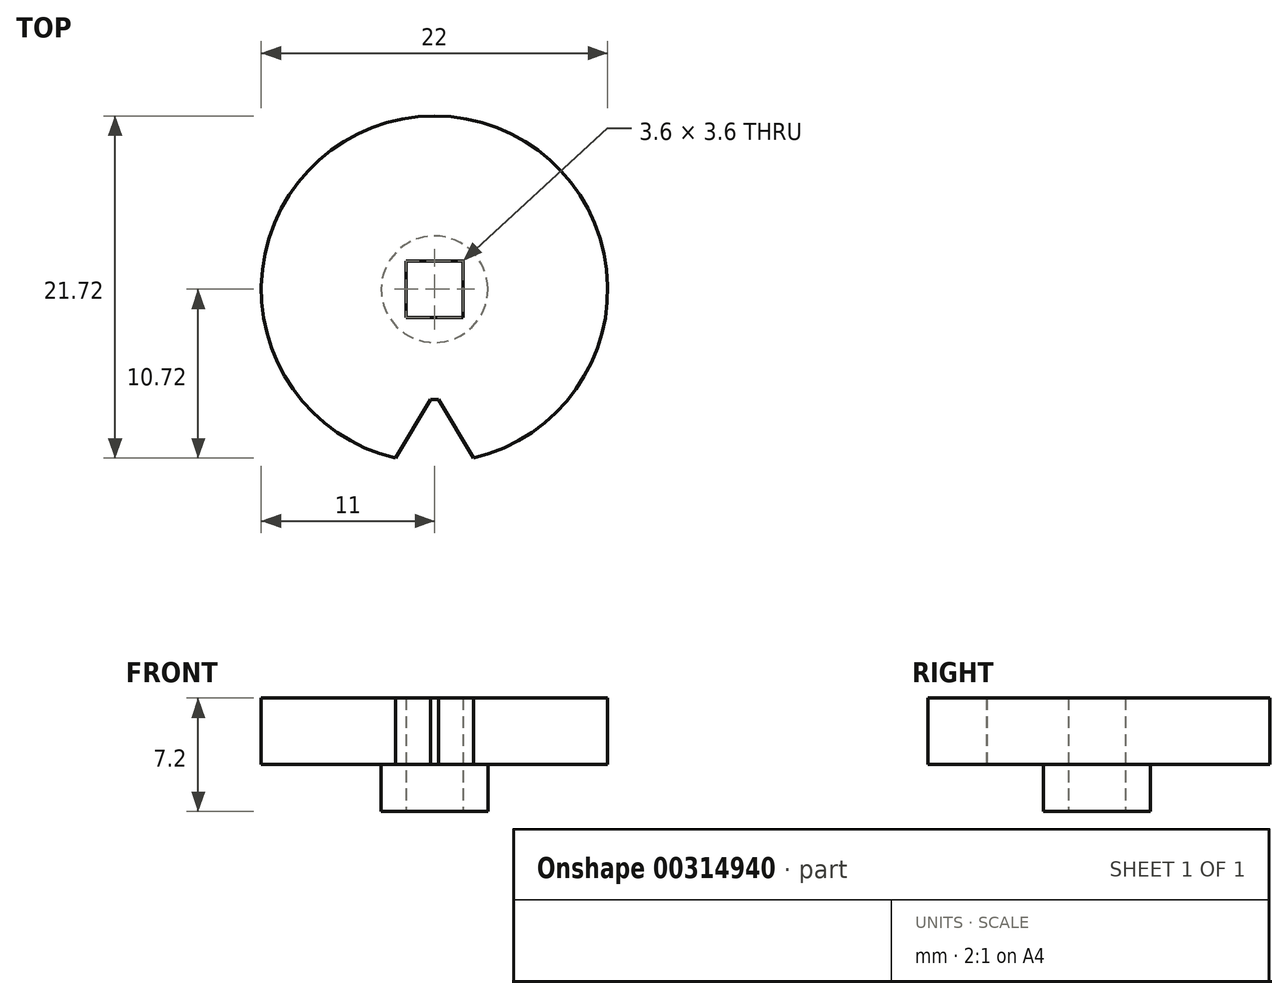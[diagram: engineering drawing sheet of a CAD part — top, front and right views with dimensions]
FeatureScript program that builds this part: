
annotation { "Feature Type Name" : "Feature", "Feature Type Description" : "" }
export const myFeature = defineFeature(function(context is Context, id is Id, definition is map)
    precondition{}
    {
        {
            var Q0;
            Q0=qCreatedBy(makeId("Top.planeOp"),FACE);
            var sketch = newSketch(context, id + "F0", { "sketchPlane" : qUnion([Q0])});
            skCircle(sketch, "E0", {"center": v(0, 0) * mm, "radius": 11 * mm});
            skSolve(sketch);
        }
        {
            var Q0;
            Q0 = qSketchRegion(id + "F0", true);
            extrude(context, id + "F1", {"entities" : qUnion([Q0]), "depth" : 4.2 * mm});
        }
        {
            var Q0;
            Q0=makeQuery(id+"F1.opExtrude","CAP_FACE",FACE,{"disambiguationData":[OSD([sQuery(id+"F0.wireOp",EDGE,"E0")])],"isStart":true});
            var sketch = newSketch(context, id + "F2", { "sketchPlane" : qUnion([Q0])});
            skLineSegment(sketch, "E1", {"start": v(0, 0) * mm, "end": v(0, 11) * mm});
            skLineSegment(sketch, "E2", {"start": v(0, 0) * mm, "end": v(-0.24, 7) * mm});
            skLineSegment(sketch, "E3", {"start": v(0, 0) * mm, "end": v(0.24, 7) * mm});
            skLineSegment(sketch, "E4", {"start": v(0, 0) * mm, "end": v(-2.47, 10.72) * mm});
            skLineSegment(sketch, "E5", {"start": v(0, 0) * mm, "end": v(2.47, 10.72) * mm});
            skArc(sketch, "E6", {"start": v(-2.47, 10.72) * mm, "mid": v(0, 11) * mm, "end": v(2.47, 10.72) * mm});
            skLineSegment(sketch, "E7", {"start": v(-0.24, 7) * mm, "end": v(-2.47, 10.72) * mm});
            skLineSegment(sketch, "E8", {"start": v(0.24, 7) * mm, "end": v(2.47, 10.72) * mm});
            skArc(sketch, "E9", {"start": v(-0.24, 7) * mm, "mid": v(0, 7) * mm, "end": v(0.24, 7) * mm});
            skSolve(sketch);
        }
        {
            var Q0;
            {var subQ5=sQuery(id+"F2.wireOp",EDGE,"E7");Q0=makeQuery(id+"F2.imprint","IMPRINT",FACE,{"disambiguationData":[TD([[makeQuery(id+"F2.imprint","IMPRINT",EDGE,{"derivedFrom":subQ5}),-1.0]])]});}
            var Q1;
            {var subQ5=sQuery(id+"F2.wireOp",EDGE,"E8");Q1=makeQuery(id+"F2.imprint","IMPRINT",FACE,{"disambiguationData":[TD([[makeQuery(id+"F2.imprint","IMPRINT",EDGE,{"derivedFrom":subQ5}),1.0]])]});}
            extrude(context, id + "F3", {"entities" : qUnion([Q0, Q1]), "operationType" : NewBodyOperationType.REMOVE, "endBound" : BoundingType.THROUGH_ALL, "oppositeDirection" : true, "depth" : 25 * mm});
        }
        {
            var Q0;
            Q0=qCreatedBy(makeId("Front.planeOp"),FACE);
            var sketch = newSketch(context, id + "F4", { "sketchPlane" : qUnion([Q0])});
            skLineSegment(sketch, "E10", {"start": v(0, 0) * mm, "end": v(0, -10.83) * mm});
            skSolve(sketch);
        }
        {
            var Q0;
            Q0=makeQuery(id+"F1.opExtrude","CAP_FACE",FACE,{"disambiguationData":[OSD([sQuery(id+"F0.wireOp",EDGE,"E0")])],"isStart":true});
            var sketch = newSketch(context, id + "F5", { "sketchPlane" : qUnion([Q0])});
            skCircle(sketch, "E11", {"center": v(0, 0) * mm, "radius": 3.39 * mm});
            skSolve(sketch);
        }
        {
            var Q0;
            Q0 = qSketchRegion(id + "F5", true);
            extrude(context, id + "F6", {"entities" : qUnion([Q0]), "operationType" : NewBodyOperationType.ADD, "depth" : 3 * mm});
        }
        {
            var Q0;
            Q0=makeQuery(id+"F6.opExtrude","CAP_FACE",FACE,{"disambiguationData":[OSD([sQuery(id+"F5.wireOp",EDGE,"E11")])],"isStart":false});
            var sketch = newSketch(context, id + "F7", { "sketchPlane" : qUnion([Q0])});
            skLineSegment(sketch, "E12.bottom", {"start": v(-1.8, -1.8) * mm, "end": v(1.8, -1.8) * mm});
            skLineSegment(sketch, "E12.top", {"start": v(-1.8, 1.8) * mm, "end": v(1.8, 1.8) * mm});
            skLineSegment(sketch, "E12.left", {"start": v(-1.8, -1.8) * mm, "end": v(-1.8, 1.8) * mm});
            skLineSegment(sketch, "E12.right", {"start": v(1.8, -1.8) * mm, "end": v(1.8, 1.8) * mm});
            skPoint(sketch, "E12.middle", {"position": v(0, 0) * mm});
            skSolve(sketch);
        }
        {
            var Q0;
            Q0 = qSketchRegion(id + "F7", true);
            extrude(context, id + "F8", {"entities" : qUnion([Q0]), "operationType" : NewBodyOperationType.REMOVE, "endBound" : BoundingType.THROUGH_ALL, "oppositeDirection" : true, "depth" : 3 * mm});
        }
    });
